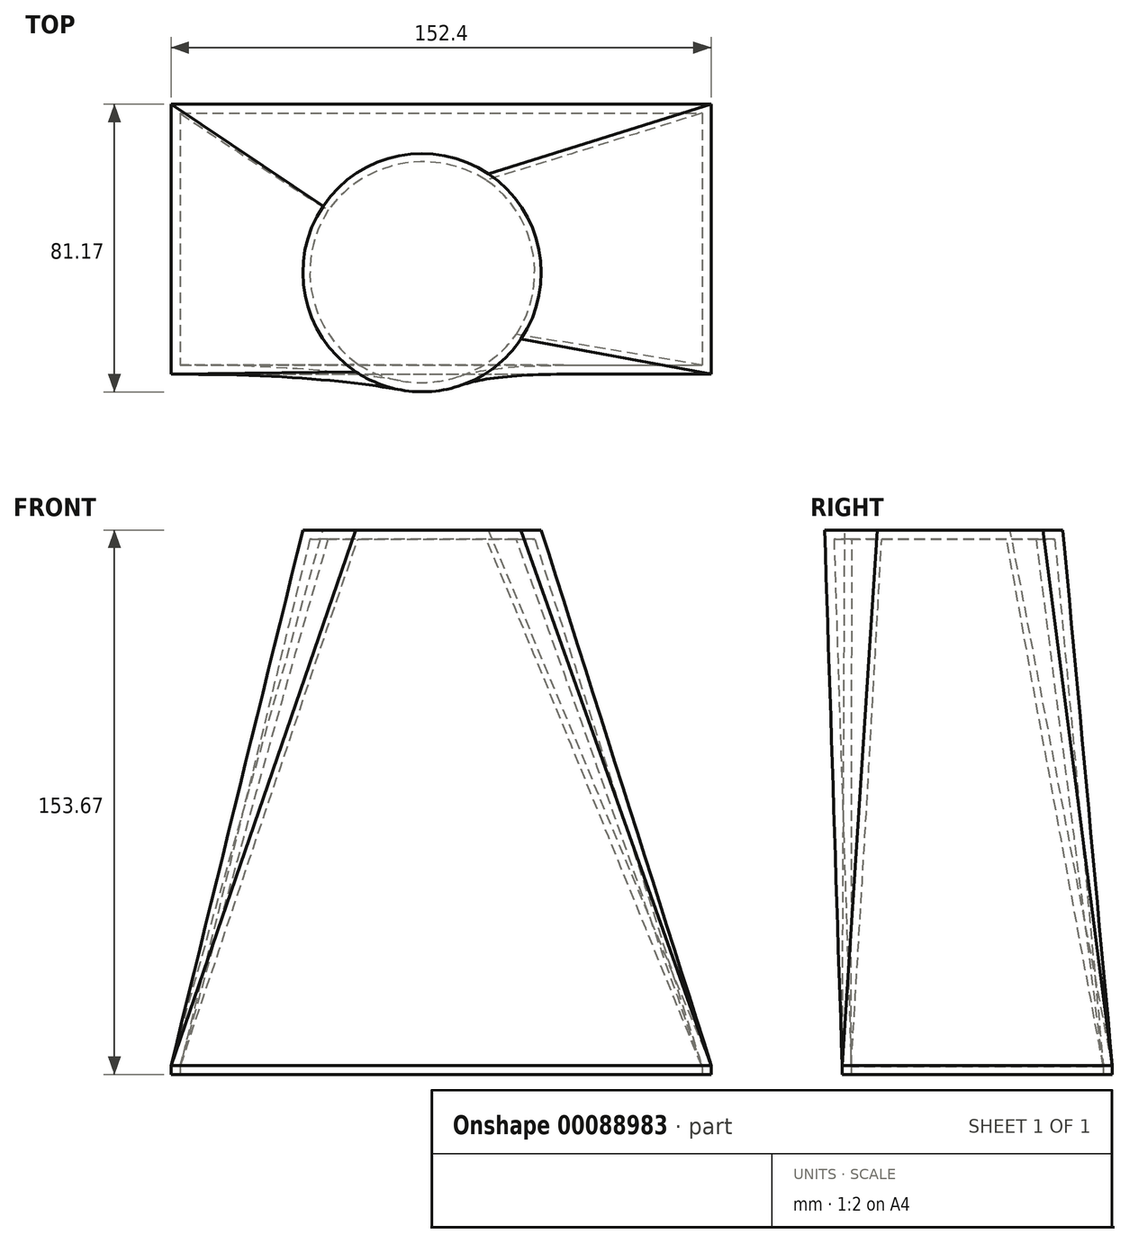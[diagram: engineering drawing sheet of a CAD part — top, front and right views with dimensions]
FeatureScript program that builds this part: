
annotation { "Feature Type Name" : "Feature", "Feature Type Description" : "" }
export const myFeature = defineFeature(function(context is Context, id is Id, definition is map)
    precondition{}
    {
        {
            var Q0;
            Q0=qCreatedBy(makeId("Top.planeOp"),FACE);
            var sketch = newSketch(context, id + "F0", { "sketchPlane" : qUnion([Q0])});
            skLineSegment(sketch, "E0.bottom", {"start": v(-76.2, 38.1) * mm, "end": v(76.2, 38.1) * mm});
            skLineSegment(sketch, "E0.top", {"start": v(-76.2, -38.1) * mm, "end": v(76.2, -38.1) * mm});
            skLineSegment(sketch, "E0.left", {"start": v(-76.2, 38.1) * mm, "end": v(-76.2, -38.1) * mm});
            skLineSegment(sketch, "E0.right", {"start": v(76.2, 38.1) * mm, "end": v(76.2, -38.1) * mm});
            skPoint(sketch, "E0.middle", {"position": v(0, 0) * mm});
            skSolve(sketch);
        }
        {
            var Q0;
            Q0=makeQuery(id+"F0.imprint","IMPRINT",FACE,{"disambiguationData":[TD([[makeQuery(id+"F0.imprint","IMPRINT",EDGE,{"derivedFrom":sQuery(id+"F0.wireOp",EDGE,"E0.bottom")}),-1.0]])]});
            extrude(context, id + "F1", {"entities" : qUnion([Q0]), "endBound" : BoundingType.SYMMETRIC, "depth" : 2.54 * mm});
        }
        {
            var Q0;
            Q0=qCreatedBy(makeId("Top.planeOp"),FACE);
            cPlane(context, id + "F2", {"entities" : qUnion([Q0]), "cplaneType" : CPlaneType.OFFSET, "offset" : 152.4 * mm, "width" : 152.4 * mm, "height" : 152.4 * mm});
        }
        {
            var Q0;
            Q0=qCreatedBy(id+"F2.planeOp",FACE);
            var sketch = newSketch(context, id + "F3", { "sketchPlane" : qUnion([Q0])});
            skCircle(sketch, "E1", {"center": v(-5.39, -9.44) * mm, "radius": 33.62 * mm});
            skSolve(sketch);
        }
        {
            var Q1;
            Q1=makeQuery(id+"F1.opExtrude","CAP_FACE",FACE,{"disambiguationData":[OSD([sQuery(id+"F0.wireOp",EDGE,"E0.bottom"),sQuery(id+"F0.wireOp",EDGE,"E0.top"),sQuery(id+"F0.wireOp",EDGE,"E0.left"),sQuery(id+"F0.wireOp",EDGE,"E0.right")])],"isStart":false});
            var Q2;
            Q2=makeQuery(id+"F3.imprint","IMPRINT",FACE,{"disambiguationData":[TD([[makeQuery(id+"F3.imprint","IMPRINT",EDGE,{"derivedFrom":sQuery(id+"F3.wireOp",EDGE,"E1")}),1.0]])]});
            loft(context, id + "F4", {"operationType" : NewBodyOperationType.ADD, "sheetProfilesArray" : [{ "sheetProfileEntities" : qUnion([Q1]) }, { "sheetProfileEntities" : qUnion([Q2]) }]});
        }
        {
            var Q0;
            Q0=makeQuery(id+"F1.opExtrude","CAP_FACE",FACE,{"disambiguationData":[OSD([sQuery(id+"F0.wireOp",EDGE,"E0.bottom"),sQuery(id+"F0.wireOp",EDGE,"E0.top"),sQuery(id+"F0.wireOp",EDGE,"E0.left"),sQuery(id+"F0.wireOp",EDGE,"E0.right")])],"isStart":true});
            shell(context, id + "F5", {"entities" : qUnion([Q0]), "thickness" : 2.54 * mm});
        }
    });
